# Revit family: Запорный клапан со встроенным обратным клапаном 4126
name_source: partatom
category: Rohrzubehör
units: mm (PartAtom-declared; Revit-internal decimal feet)

## family parameters
Arbeitsebenenbasiert = Nein
Beim Laden mit Abzugskörper schneiden = Nein
Bemaßung runder Anschluss = Durchmesser verwenden
Gemeinsam genutzt = Nein
Immer vertikal = Ja
OmniClass-Nummer = 23.65.55.14
OmniClass-Titel = Valves for Liquid Services
Teiletyp = Unterbricht

## types (1)
- Запорный клапан со встроенным обратным клапаном 4126
    Hersteller = HERZ Armaturen Ges.m.b.H.
    L03 = 15 mm
    R03 = 9.5 mm  [stored 0.031168 ft]
    R100 = 1 mm  [stored 0.00328084 ft]
    S03 = 60 mm
    SCTWCODE = 04;00;02
    SCTWSEQ = FW;SBT_TYP_FW="109";2
    SC_NennweiteBerechnet = 0
    SW01 = 60.00°
    URL = www.herz-armaturen.ru
    Vorgabe-Ansicht = 0 mm  [stored 0 ft]
    W01 = 45.00°
    Давление открытия обратного клапана = согласно DIN EN 13959
    Конус = штампованная латунь, CW617N
    Корпус = литая латунь, устойчивая к селективной цинковой коррозии, CC770S
    Макс. перепад давления на закрытом седле = 1000000.0 Pa
    Макс. рабочая температура = 80 °C
    Макс. рабочее давление = 1600000.0 Pa
    Маховик = пластик, цвет - зеленый
    Незапланированные повышения температуры = до  95 °C, продолжительностью не более 1 часа
    Область применения = Для перекрытия трубопроводов системы питьевого водоснабжения и циркуляционных систем в зданиях.
    Примечание = В соответствии со статьей 33 Регламента REACH (Registration; Evaluation; Authorisation; Restriction of Chemicals) (EC № 1907/2006) мы обязаны указать, что свинец внесен в список SVHC (Substances of Very High Concern - вещества очень высокой важности) и весовой процент свинца во всех латунных компонентах заводского изготовления в наших изделиях, превышает 0,1 % (w/w) (CAS: 7439-92-1 / EINECS: 231-100-4).
Поскольку свинец является легирующим компонентом сплава, прямое негативное влияние исключается, и поэтому дополнительной информации о безопасном использовании не требуется.
    Среда = питьевая вода
    Шпиндель = штампованная латунь, CW617N

note: [stored X ft] marks values corroborated as IEEE doubles in the binary element streams (Revit-internal decimal feet)
